# Revit family: Valve-Sink_Supply-KOHLER-K-R76389T
name_source: partatom
category: Plumbing Fixtures
units: mm (PartAtom-declared; Revit-internal decimal feet)

## family parameters
Cut with Voids When Loaded = No
Host = Face
OmniClass Number = 23.27.31.00
OmniClass Title = Valves
Part Type = Normal
Room Calculation Point = No
Round Connector Dimension = Use Diameter
Shared = No

## types (4) — shared parameters
ADA Compliant = No
Assembly Code = D2020
CW Connection = Yes
Cold Water Inlet = Cold Water Inlet
Cold Water Outlet = Cold Water Outlet
Date Modified = 01/05/2024
Default Elevation = 36"
Flow Rate = 0 GPM
HW Connection = No
Hot Water Inlet = Hot Water Inlet
Length = 15/16"
Manufacturer = Kohler Co.
Master Format 2014 = 23 09 13.33
Master Format 2014 Name = Control Valves
Material = Premium Metal Construction
Pressure = 0.00 psi
URL = http://www.kohler.com.cn
Vent Connection = No
Waste Connection = No
Waste Water Outlet = Waste Water Outlet
WaterSense Certified = No

## per-type parameters (varying)
| type | 9_ | B9 | Description | Finish | Height | Model | Product Documentation Link | Product Page URL | Type |
| 9, CP-Polished Chrome | Yes | No | Angle Valve One Piece | Kohler-Metal-CP-Polished_Chrome | 1 9/16" | K-R76389T-9-CP | https://files.kohler.com.cn | https://www.kohler.com.cn | 2 |
| B9, BL-Matte Black | No | Yes | Angle Valve One Piece | Kohler-Metal-BL-Matte_Black | 2 3/16" | K-R76389T-B9-BL |  |  | 3 |
| B9, CP-Polished Chrome | No | Yes | Angle Valve One Piece | Kohler-Metal-CP-Polished_Chrome | 2 3/16" | K-R76389T-B9-CP |  |  | 4 |
| 9, BL-Matte Black | Yes | No | Angle valve (1 pack/retail pack) | Kohler-Metal-BL-Matte_Black | 1 9/16" | K-R76389T-9-BL | https://files.kohler.com.cn | https://www.kohler.com.cn | 1 |

## geometry (parser evidence)
native form markers: Sweep x4
no freeform markers — native parametric forms only
